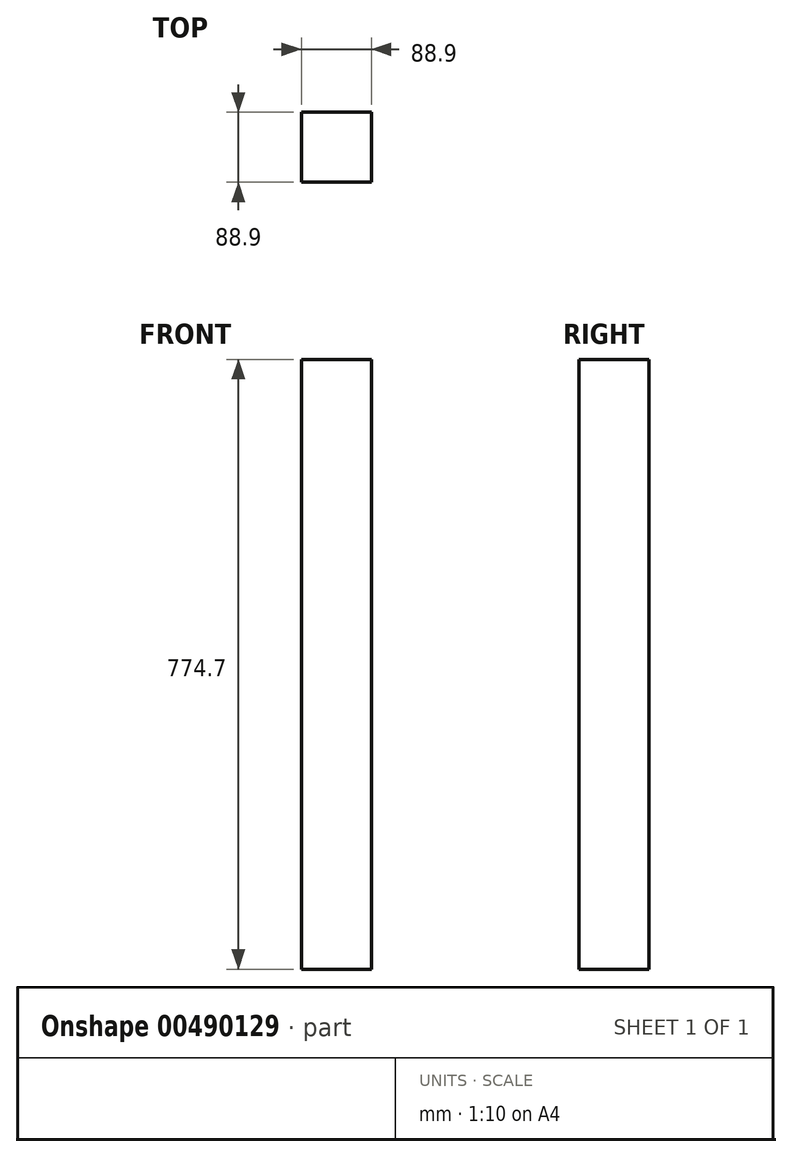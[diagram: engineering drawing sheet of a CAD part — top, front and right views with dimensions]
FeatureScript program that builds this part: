
annotation { "Feature Type Name" : "Feature", "Feature Type Description" : "" }
export const myFeature = defineFeature(function(context is Context, id is Id, definition is map)
    precondition{}
    {
        {
            var Q0;
            Q0=qCreatedBy(makeId("Top.planeOp"),FACE);
            var sketch = newSketch(context, id + "F0", { "sketchPlane" : qUnion([Q0])});
            skLineSegment(sketch, "E0.bottom", {"start": v(44.45, 44.45) * mm, "end": v(-44.45, 44.45) * mm});
            skLineSegment(sketch, "E0.top", {"start": v(44.45, -44.45) * mm, "end": v(-44.45, -44.45) * mm});
            skLineSegment(sketch, "E0.left", {"start": v(44.45, 44.45) * mm, "end": v(44.45, -44.45) * mm});
            skLineSegment(sketch, "E0.right", {"start": v(-44.45, 44.45) * mm, "end": v(-44.45, -44.45) * mm});
            skPoint(sketch, "E0.middle", {"position": v(0, 0) * mm});
            skSolve(sketch);
        }
        {
            var Q0;
            Q0=makeQuery(id+"F0.imprint","IMPRINT",FACE,{"disambiguationData":[TD([[makeQuery(id+"F0.imprint","IMPRINT",EDGE,{"derivedFrom":sQuery(id+"F0.wireOp",EDGE,"E0.bottom")}),1.0]])]});
            extrude(context, id + "F1", {"entities" : qUnion([Q0]), "oppositeDirection" : true, "depth" : 774.7 * mm, "offsetDistance" : 25.4 * mm});
        }
    });
